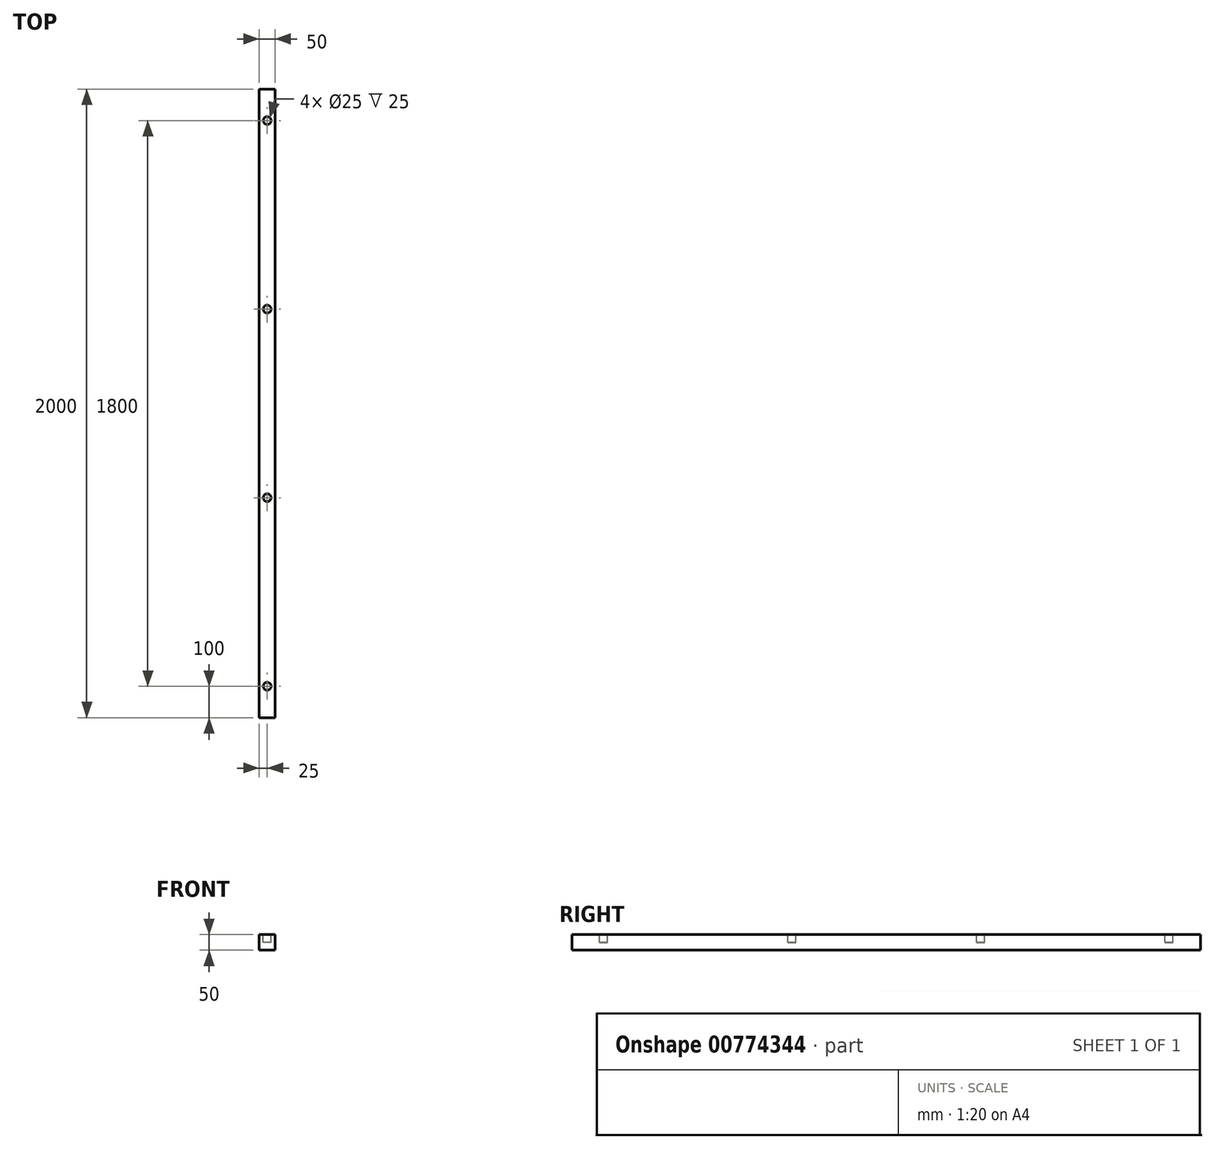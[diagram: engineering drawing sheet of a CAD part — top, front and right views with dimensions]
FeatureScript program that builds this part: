
annotation { "Feature Type Name" : "Feature", "Feature Type Description" : "" }
export const myFeature = defineFeature(function(context is Context, id is Id, definition is map)
    precondition{}
    {
        {
            var Q0;
            Q0=qCreatedBy(makeId("Front.planeOp"),FACE);
            var sketch = newSketch(context, id + "F0", { "sketchPlane" : qUnion([Q0])});
            skLineSegment(sketch, "E0.bottom", {"start": v(0, 0) * mm, "end": v(50, 0) * mm});
            skLineSegment(sketch, "E0.top", {"start": v(0, 50) * mm, "end": v(50, 50) * mm});
            skLineSegment(sketch, "E0.left", {"start": v(0, 0) * mm, "end": v(0, 50) * mm});
            skLineSegment(sketch, "E0.right", {"start": v(50, 0) * mm, "end": v(50, 50) * mm});
            skSolve(sketch);
        }
        {
            var Q0;
            Q0=makeQuery(id+"F0.imprint","IMPRINT",FACE,{"disambiguationData":[TD([[makeQuery(id+"F0.imprint","IMPRINT",EDGE,{"derivedFrom":sQuery(id+"F0.wireOp",EDGE,"E0.bottom")}),1.0]])]});
            extrude(context, id + "F1", {"entities" : qUnion([Q0]), "oppositeDirection" : true, "depth" : 2000 * mm, "offsetDistance" : 25 * mm});
        }
        {
            var Q0;
            Q0=makeQuery(id+"F1.opExtrude","SWEPT_FACE",FACE,{"disambiguationData":[OSD([sQuery(id+"F0.wireOp",EDGE,"E0.top")])]});
            var sketch = newSketch(context, id + "F2", { "sketchPlane" : qUnion([Q0])});
            skCircle(sketch, "E1", {"center": v(25, 100) * mm, "radius": 12.5 * mm});
            skPoint(sketch, "E1.centerSnap0", {"position": v(25, 0) * mm});
            skCircle(sketch, "E2.0.1.0", {"center": v(25, 700) * mm, "radius": 12.5 * mm});
            skLineSegment(sketch, "E2.direction1", {"start": v(25, 100) * mm, "end": v(110, 100) * mm, "construction": true});
            skLineSegment(sketch, "E2.direction2", {"start": v(25, 100) * mm, "end": v(25, 700) * mm, "construction": true});
            skCircle(sketch, "E3.0.0.2", {"center": v(25, 1300) * mm, "radius": 12.5 * mm});
            skCircle(sketch, "E3.0.0.3", {"center": v(25, 1900) * mm, "radius": 12.5 * mm});
            skSolve(sketch);
        }
        {
            var Q0;
            Q0=makeQuery(id+"F2.imprint","IMPRINT",FACE,{"disambiguationData":[TD([[makeQuery(id+"F2.imprint","IMPRINT",EDGE,{"derivedFrom":sQuery(id+"F2.wireOp",EDGE,"E1")}),1.0]])]});
            var Q1;
            Q1=makeQuery(id+"F2.imprint","IMPRINT",FACE,{"disambiguationData":[TD([[makeQuery(id+"F2.imprint","IMPRINT",EDGE,{"derivedFrom":sQuery(id+"F2.wireOp",EDGE,"E3.0.0.3")}),1.0]])]});
            var Q2;
            Q2=makeQuery(id+"F2.imprint","IMPRINT",FACE,{"disambiguationData":[TD([[makeQuery(id+"F2.imprint","IMPRINT",EDGE,{"derivedFrom":sQuery(id+"F2.wireOp",EDGE,"E3.0.0.2")}),1.0]])]});
            var Q3;
            Q3=makeQuery(id+"F2.imprint","IMPRINT",FACE,{"disambiguationData":[TD([[makeQuery(id+"F2.imprint","IMPRINT",EDGE,{"derivedFrom":sQuery(id+"F2.wireOp",EDGE,"E2.0.1.0")}),1.0]])]});
            extrude(context, id + "F3", {"entities" : qUnion([Q0, Q1, Q2, Q3]), "operationType" : NewBodyOperationType.REMOVE, "oppositeDirection" : true, "depth" : 25 * mm, "offsetDistance" : 25 * mm});
        }
    });
